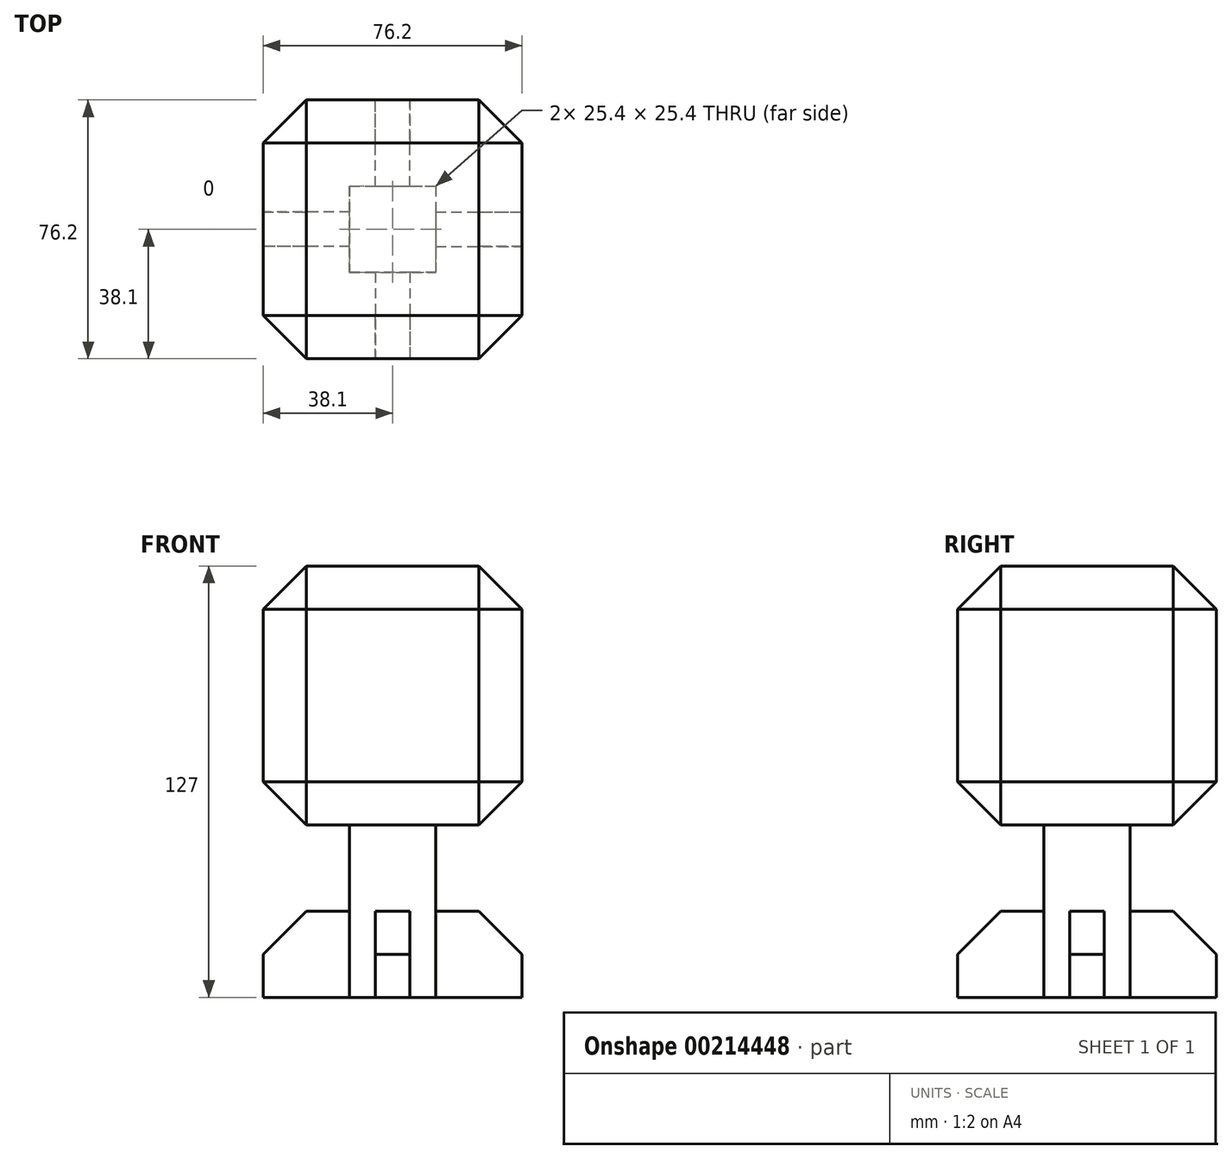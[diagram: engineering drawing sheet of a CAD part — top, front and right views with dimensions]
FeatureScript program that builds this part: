
annotation { "Feature Type Name" : "Feature", "Feature Type Description" : "" }
export const myFeature = defineFeature(function(context is Context, id is Id, definition is map)
    precondition{}
    {
        {
            var Q0;
            Q0=qCreatedBy(makeId("Top.planeOp"),FACE);
            var sketch = newSketch(context, id + "F0", { "sketchPlane" : qUnion([Q0])});
            skLineSegment(sketch, "E0.bottom", {"start": v(12.7, 12.7) * mm, "end": v(-12.7, 12.7) * mm});
            skLineSegment(sketch, "E0.top", {"start": v(12.7, -12.7) * mm, "end": v(-12.7, -12.7) * mm});
            skLineSegment(sketch, "E0.left", {"start": v(12.7, 12.7) * mm, "end": v(12.7, -12.7) * mm});
            skLineSegment(sketch, "E0.right", {"start": v(-12.7, 12.7) * mm, "end": v(-12.7, -12.7) * mm});
            skPoint(sketch, "E0.middle", {"position": v(0, 0) * mm});
            skSolve(sketch);
        }
        {
            var Q0;
            Q0 = qSketchRegion(id + "F0", true);
            extrude(context, id + "F1", {"entities" : qUnion([Q0]), "depth" : 50.8 * mm});
        }
        {
            var Q0;
            Q0=qCreatedBy(makeId("Top.planeOp"),FACE);
            cPlane(context, id + "F2", {"entities" : qUnion([Q0]), "cplaneType" : CPlaneType.OFFSET, "offset" : 50.8 * mm, "width" : 152.4 * mm, "height" : 152.4 * mm});
        }
        {
            var Q0;
            Q0=qCreatedBy(id+"F2.planeOp",FACE);
            var sketch = newSketch(context, id + "F3", { "sketchPlane" : qUnion([Q0])});
            skLineSegment(sketch, "E1.bottom", {"start": v(38.1, 38.1) * mm, "end": v(-38.1, 38.1) * mm});
            skLineSegment(sketch, "E1.top", {"start": v(38.1, -38.1) * mm, "end": v(-38.1, -38.1) * mm});
            skLineSegment(sketch, "E1.left", {"start": v(38.1, 38.1) * mm, "end": v(38.1, -38.1) * mm});
            skLineSegment(sketch, "E1.right", {"start": v(-38.1, 38.1) * mm, "end": v(-38.1, -38.1) * mm});
            skPoint(sketch, "E1.middle", {"position": v(0, 0) * mm});
            skSolve(sketch);
        }
        {
            var Q0;
            Q0=makeQuery(id+"F3.imprint","IMPRINT",FACE,{"disambiguationData":[TD([[makeQuery(id+"F3.imprint","IMPRINT",EDGE,{"derivedFrom":sQuery(id+"F3.wireOp",EDGE,"E1.bottom")}),1.0]])]});
            extrude(context, id + "F4", {"entities" : qUnion([Q0]), "operationType" : NewBodyOperationType.ADD, "depth" : 76.2 * mm});
        }
        {
            var Q0;
            Q0=makeQuery(id+"F4.opExtrude","SWEPT_EDGE",EDGE,{"disambiguationData":[OSD([sQuery(id+"F3.wireOp",EDGE,"E1.top"),sQuery(id+"F3.wireOp",EDGE,"E1.left")])]});
            var Q1;
            Q1=makeQuery(id+"F4.opExtrude","SWEPT_EDGE",EDGE,{"disambiguationData":[OSD([sQuery(id+"F3.wireOp",EDGE,"E1.bottom"),sQuery(id+"F3.wireOp",EDGE,"E1.left")])]});
            var Q2;
            Q2=makeQuery(id+"F4.opExtrude","SWEPT_EDGE",EDGE,{"disambiguationData":[OSD([sQuery(id+"F3.wireOp",EDGE,"E1.bottom"),sQuery(id+"F3.wireOp",EDGE,"E1.right")])]});
            var Q3;
            Q3=makeQuery(id+"F4.opExtrude","SWEPT_EDGE",EDGE,{"disambiguationData":[OSD([sQuery(id+"F3.wireOp",EDGE,"E1.top"),sQuery(id+"F3.wireOp",EDGE,"E1.right")])]});
            var Q4;
            Q4=makeQuery(id+"F4.opExtrude","CAP_EDGE",EDGE,{"disambiguationData":[OSD([sQuery(id+"F3.wireOp",EDGE,"E1.top")])],"isStart":false});
            var Q5;
            Q5=makeQuery(id+"F4.opExtrude","CAP_EDGE",EDGE,{"disambiguationData":[OSD([sQuery(id+"F3.wireOp",EDGE,"E1.left")])],"isStart":false});
            var Q6;
            Q6=makeQuery(id+"F4.opExtrude","CAP_EDGE",EDGE,{"disambiguationData":[OSD([sQuery(id+"F3.wireOp",EDGE,"E1.bottom")])],"isStart":false});
            var Q7;
            Q7=makeQuery(id+"F4.opExtrude","CAP_FACE",FACE,{"disambiguationData":[OSD([sQuery(id+"F3.wireOp",EDGE,"E1.bottom"),sQuery(id+"F3.wireOp",EDGE,"E1.top"),sQuery(id+"F3.wireOp",EDGE,"E1.left"),sQuery(id+"F3.wireOp",EDGE,"E1.right")])],"isStart":false});
            var Q8;
            Q8=makeQuery(id+"F4.opExtrude","CAP_EDGE",EDGE,{"disambiguationData":[OSD([sQuery(id+"F3.wireOp",EDGE,"E1.bottom")])],"isStart":true});
            var Q9;
            Q9=makeQuery(id+"F4.opExtrude","CAP_EDGE",EDGE,{"disambiguationData":[OSD([sQuery(id+"F3.wireOp",EDGE,"E1.left")])],"isStart":true});
            var Q10;
            Q10=makeQuery(id+"F4.opExtrude","CAP_EDGE",EDGE,{"disambiguationData":[OSD([sQuery(id+"F3.wireOp",EDGE,"E1.top")])],"isStart":true});
            var Q11;
            Q11=makeQuery(id+"F4.opExtrude","CAP_EDGE",EDGE,{"disambiguationData":[OSD([sQuery(id+"F3.wireOp",EDGE,"E1.right")])],"isStart":true});
            chamfer(context, id + "F5", {"entities" : qUnion([Q0, Q1, Q2, Q3, Q4, Q5, Q6, Q7, Q8, Q9, Q10, Q11]), "width" : 12.7 * mm, "tangentPropagation" : true});
        }
        {
            var Q0;
            Q0=qCreatedBy(makeId("Right.planeOp"),FACE);
            var sketch = newSketch(context, id + "F6", { "sketchPlane" : qUnion([Q0])});
            skLineSegment(sketch, "E2.bottom", {"start": v(-12.7, 0) * mm, "end": v(-38.1, 0) * mm});
            skLineSegment(sketch, "E2.top", {"start": v(-12.7, 25.4) * mm, "end": v(-38.1, 25.4) * mm});
            skLineSegment(sketch, "E2.left", {"start": v(-12.7, 0) * mm, "end": v(-12.7, 25.4) * mm});
            skLineSegment(sketch, "E2.right", {"start": v(-38.1, 0) * mm, "end": v(-38.1, 25.4) * mm});
            skSolve(sketch);
        }
        {
            var Q0;
            Q0 = qSketchRegion(id + "F6", true);
            extrude(context, id + "F7", {"entities" : qUnion([Q0]), "operationType" : NewBodyOperationType.ADD, "depth" : 5.08 * mm, "hasSecondDirection" : true, "secondDirectionOppositeDirection" : true, "secondDirectionDepth" : 5.08 * mm});
        }
        {
            var Q0;
            Q0=qCreatedBy(makeId("Right.planeOp"),FACE);
            var sketch = newSketch(context, id + "F8", { "sketchPlane" : qUnion([Q0])});
            skLineSegment(sketch, "E3", {"start": v(0, -1.85) * mm, "end": v(0, -31.18) * mm, "construction": true});
            skSolve(sketch);
        }
        {
            var Q0;
            Q0=makeQuery(id+"F1.opExtrude","SWEPT_BODY",BODY,{"disambiguationData":[OSD([sQuery(id+"F0.wireOp",EDGE,"E0.bottom"),sQuery(id+"F0.wireOp",EDGE,"E0.top"),sQuery(id+"F0.wireOp",EDGE,"E0.left"),sQuery(id+"F0.wireOp",EDGE,"E0.right")])]});
            var Q1;
            Q1=sQuery(id+"F8.wireOp",EDGE,"E3");
            circularPattern(context, id + "F9", {"entities" : qUnion([Q0]), "axis" : qUnion([Q1]), "angle" : 360 * degree, "instanceCount" : 4, "equalSpace" : true});
        }
        {
            var Q0;
            Q0=makeQuery(id+"F7.opExtrude","SWEPT_EDGE",EDGE,{"disambiguationData":[OSD([sQuery(id+"F6.wireOp",EDGE,"E2.top"),sQuery(id+"F6.wireOp",EDGE,"E2.right")])]});
            var Q1;
            Q1=makeQuery(id+"F9.opPattern","COPY",EDGE,{"derivedFrom":makeQuery(id+"F7.opExtrude","SWEPT_EDGE",EDGE,{"disambiguationData":[OSD([sQuery(id+"F6.wireOp",EDGE,"E2.top"),sQuery(id+"F6.wireOp",EDGE,"E2.right")])]}),"instanceName":"3"});
            var Q2;
            Q2=makeQuery(id+"F9.opPattern","COPY",EDGE,{"derivedFrom":makeQuery(id+"F7.opExtrude","SWEPT_EDGE",EDGE,{"disambiguationData":[OSD([sQuery(id+"F6.wireOp",EDGE,"E2.top"),sQuery(id+"F6.wireOp",EDGE,"E2.right")])]}),"instanceName":"2"});
            var Q3;
            Q3=makeQuery(id+"F9.opPattern","COPY",EDGE,{"derivedFrom":makeQuery(id+"F7.opExtrude","SWEPT_EDGE",EDGE,{"disambiguationData":[OSD([sQuery(id+"F6.wireOp",EDGE,"E2.top"),sQuery(id+"F6.wireOp",EDGE,"E2.right")])]}),"instanceName":"1"});
            chamfer(context, id + "F10", {"entities" : qUnion([Q0, Q1, Q2, Q3]), "width" : 12.7 * mm, "tangentPropagation" : true});
        }
    });
